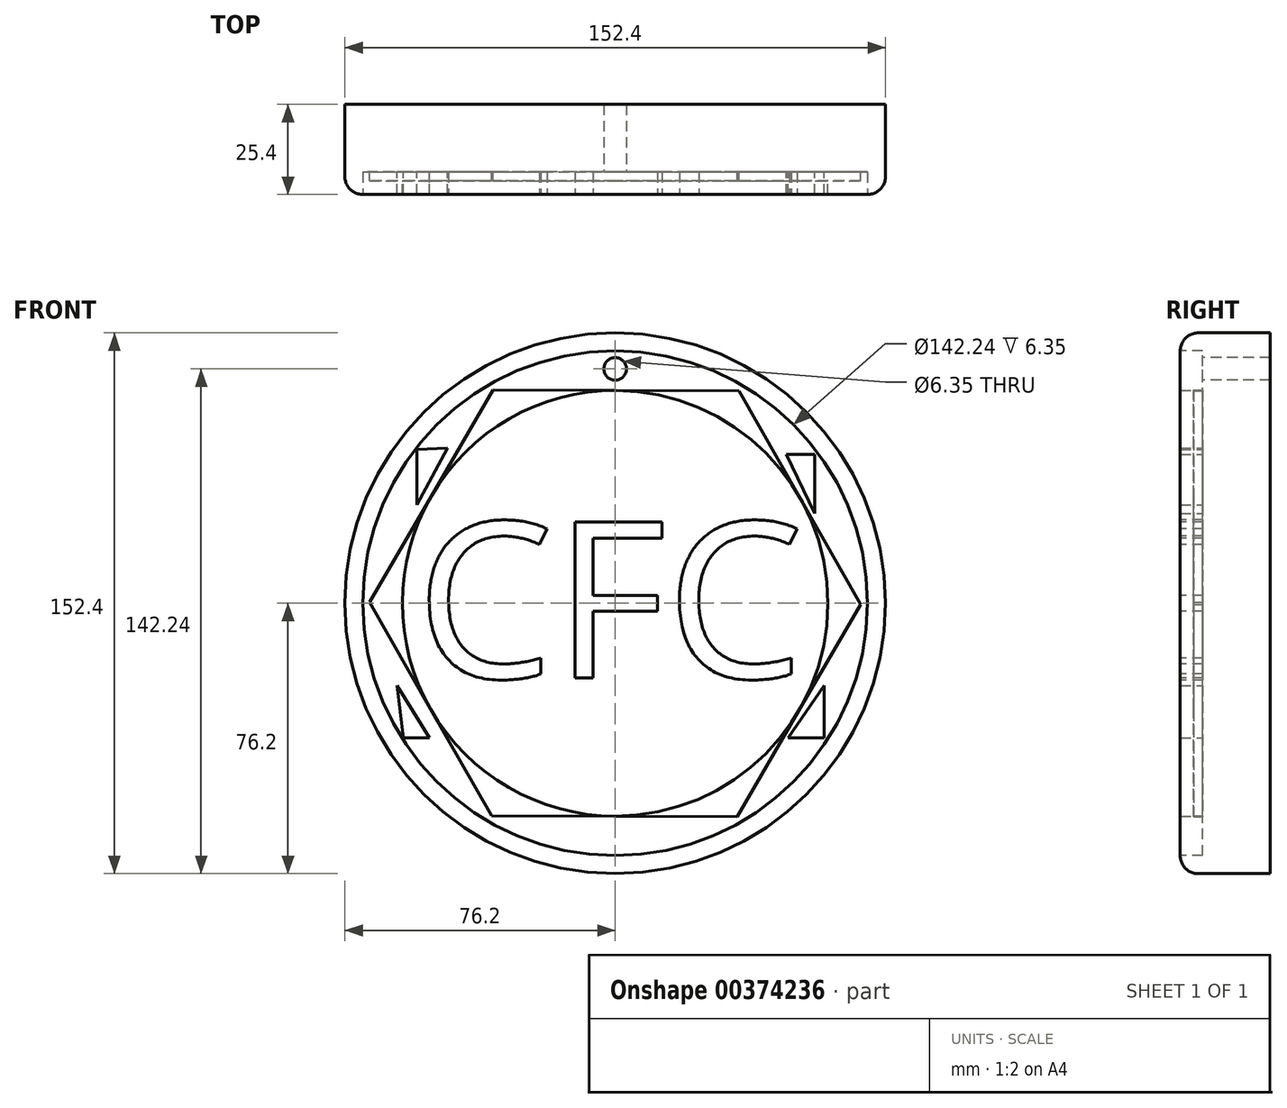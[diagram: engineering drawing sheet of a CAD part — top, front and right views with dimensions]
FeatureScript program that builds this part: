
annotation { "Feature Type Name" : "Feature", "Feature Type Description" : "" }
export const myFeature = defineFeature(function(context is Context, id is Id, definition is map)
    precondition{}
    {
        {
            var Q0;
            Q0=qCreatedBy(makeId("Front.planeOp"),FACE);
            var sketch = newSketch(context, id + "F0", { "sketchPlane" : qUnion([Q0])});
            skCircle(sketch, "E0", {"center": v(0, 0) * mm, "radius": 76.2 * mm});
            skSolve(sketch);
        }
        {
            var Q0;
            Q0 = qSketchRegion(id + "F0", true);
            extrude(context, id + "F1", {"entities" : qUnion([Q0]), "depth" : 25.4 * mm});
        }
        {
            var Q0;
            Q0=makeQuery(id+"F1.opExtrude","CAP_FACE",FACE,{"disambiguationData":[OSD([sQuery(id+"F0.wireOp",EDGE,"E0")])],"isStart":false});
            fillet(context, id + "F2", {"entities" : qUnion([Q0]), "radius" : 5.08 * mm, "tangentPropagation" : true, "allowEdgeOverflow" : false});
        }
        {
            var Q0;
            Q0=makeQuery(id+"F1.opExtrude","CAP_FACE",FACE,{"disambiguationData":[OSD([sQuery(id+"F0.wireOp",EDGE,"E0")])],"isStart":false});
            extrude(context, id + "F3", {"entities" : qUnion([Q0]), "operationType" : NewBodyOperationType.REMOVE, "oppositeDirection" : true, "depth" : 6.35 * mm});
        }
        {
            var Q0;
            Q0=makeQuery(id+"F3.boolean.opBoolean","COPY",FACE,{"derivedFrom":makeQuery(id+"F3.opExtrude","CAP_FACE",FACE,{"disambiguationData":[OSD([sQuery(id+"F0.wireOp",EDGE,"E0")])],"isStart":false})});
            var sketch = newSketch(context, id + "F4", { "sketchPlane" : qUnion([Q0])});
            skLineSegment(sketch, "E1", {"start": v(0, 0) * mm, "end": v(0, 66.04) * mm});
            skCircle(sketch, "E2", {"center": v(0, 66.04) * mm, "radius": 3.18 * mm});
            skSolve(sketch);
        }
        {
            var Q0;
            Q0=makeQuery(id+"F4.imprint","IMPRINT",FACE,{"disambiguationData":[TD([[makeQuery(id+"F4.imprint","IMPRINT",EDGE,{"derivedFrom":sQuery(id+"F4.wireOp",EDGE,"E2")}),-1.0]])]});
            var sketch = newSketch(context, id + "F5", { "sketchPlane" : qUnion([Q0])});
            skCircle(sketch, "E3.cCircle", {"center": v(0, 0) * mm, "radius": 59.98 * mm, "construction": true});
            skLineSegment(sketch, "E3.0", {"start": v(34.87, 59.84) * mm, "end": v(69.26, -0.28) * mm});
            skLineSegment(sketch, "E3.1", {"start": v(69.26, -0.28) * mm, "end": v(34.39, -60.12) * mm});
            skLineSegment(sketch, "E3.2", {"start": v(34.39, -60.12) * mm, "end": v(-34.87, -59.84) * mm});
            skLineSegment(sketch, "E3.3", {"start": v(-34.87, -59.84) * mm, "end": v(-69.26, 0.28) * mm});
            skLineSegment(sketch, "E3.4", {"start": v(-69.26, 0.28) * mm, "end": v(-34.39, 60.12) * mm});
            skLineSegment(sketch, "E3.5", {"start": v(-34.39, 60.12) * mm, "end": v(34.87, 59.84) * mm});
            skPoint(sketch, "E3.0.midPoint", {"position": v(52.06, 29.78) * mm});
            skSolve(sketch);
        }
        {
            var Q0;
            Q0 = qSketchRegion(id + "F5", true);
            extrude(context, id + "F6", {"entities" : qUnion([Q0]), "operationType" : NewBodyOperationType.ADD, "depth" : 2.54 * mm});
        }
        {
            var Q0;
            Q0=makeQuery(id+"F6.opExtrude","CAP_FACE",FACE,{"disambiguationData":[OSD([sQuery(id+"F5.wireOp",EDGE,"E3.0"),sQuery(id+"F5.wireOp",EDGE,"E3.1"),sQuery(id+"F5.wireOp",EDGE,"E3.2"),sQuery(id+"F5.wireOp",EDGE,"E3.3"),sQuery(id+"F5.wireOp",EDGE,"E3.4"),sQuery(id+"F5.wireOp",EDGE,"E3.5")])],"isStart":false});
            var sketch = newSketch(context, id + "F7", { "sketchPlane" : qUnion([Q0])});
            skCircle(sketch, "E4", {"center": v(0, 0) * mm, "radius": 59.98 * mm});
            skSolve(sketch);
        }
        {
            var Q0;
            Q0 = qSketchRegion(id + "F7", true);
            extrude(context, id + "F8", {"entities" : qUnion([Q0]), "operationType" : NewBodyOperationType.ADD, "depth" : 3.8 * mm});
        }
        {
            var Q0;
            Q0=makeQuery(id+"F4.imprint","IMPRINT",FACE,{"disambiguationData":[TD([[makeQuery(id+"F4.imprint","IMPRINT",EDGE,{"derivedFrom":sQuery(id+"F4.wireOp",EDGE,"E2")}),-1.0]])]});
            var sketch = newSketch(context, id + "F9", { "sketchPlane" : qUnion([Q0])});
            skLineSegment(sketch, "E5", {"start": v(-55.9, 43.39) * mm, "end": v(-55.9, 27.7) * mm});
            skLineSegment(sketch, "E6", {"start": v(-55.9, 27.7) * mm, "end": v(-47.33, 43.68) * mm});
            skLineSegment(sketch, "E7", {"start": v(-47.33, 43.68) * mm, "end": v(-55.9, 43.39) * mm});
            skLineSegment(sketch, "E8", {"start": v(-61.52, -23.17) * mm, "end": v(-52.35, -37.96) * mm});
            skLineSegment(sketch, "E9", {"start": v(-52.35, -37.96) * mm, "end": v(-59.75, -37.96) * mm});
            skLineSegment(sketch, "E10", {"start": v(-59.75, -37.96) * mm, "end": v(-61.52, -23.17) * mm});
            skLineSegment(sketch, "E11", {"start": v(48.81, -37.96) * mm, "end": v(58.87, -37.96) * mm});
            skLineSegment(sketch, "E12", {"start": v(58.87, -37.96) * mm, "end": v(58.87, -23.17) * mm});
            skLineSegment(sketch, "E13", {"start": v(58.87, -23.17) * mm, "end": v(48.81, -37.96) * mm});
            skLineSegment(sketch, "E14", {"start": v(48.22, 41.9) * mm, "end": v(56.2, 41.9) * mm});
            skLineSegment(sketch, "E15", {"start": v(56.2, 41.9) * mm, "end": v(56.2, 25.34) * mm});
            skLineSegment(sketch, "E16", {"start": v(56.2, 25.34) * mm, "end": v(48.22, 41.9) * mm});
            skSolve(sketch);
        }
        {
            var Q0;
            Q0=makeQuery(id+"F9.imprint","IMPRINT",FACE,{"disambiguationData":[TD([[makeQuery(id+"F9.imprint","IMPRINT",EDGE,{"derivedFrom":sQuery(id+"F9.wireOp",EDGE,"E5")}),1.0]])]});
            var Q1;
            Q1=makeQuery(id+"F9.imprint","IMPRINT",FACE,{"disambiguationData":[TD([[makeQuery(id+"F9.imprint","IMPRINT",EDGE,{"derivedFrom":sQuery(id+"F9.wireOp",EDGE,"E8")}),-1.0]])]});
            var Q2;
            Q2=makeQuery(id+"F9.imprint","IMPRINT",FACE,{"disambiguationData":[TD([[makeQuery(id+"F9.imprint","IMPRINT",EDGE,{"derivedFrom":sQuery(id+"F9.wireOp",EDGE,"E14")}),-1.0]])]});
            var Q3;
            Q3=makeQuery(id+"F9.imprint","IMPRINT",FACE,{"disambiguationData":[TD([[makeQuery(id+"F9.imprint","IMPRINT",EDGE,{"derivedFrom":sQuery(id+"F9.wireOp",EDGE,"E11")}),1.0]])]});
            extrude(context, id + "F10", {"entities" : qUnion([Q0, Q1, Q2, Q3]), "operationType" : NewBodyOperationType.ADD, "depth" : 6.35 * mm});
        }
        {
            var Q0;
            Q0=makeQuery(id+"F8.opExtrude","CAP_FACE",FACE,{"disambiguationData":[OSD([sQuery(id+"F7.wireOp",EDGE,"E4")])],"isStart":false});
            var sketch = newSketch(context, id + "F11", { "sketchPlane" : qUnion([Q0])});
            skText(sketch, "E17", { "text": "CFC", "fontName": "OpenSans-Regular.ttf"});
            const initialGuessF11  = {"E17": [-0.05617, -0.02103, 1, 0, 0.04427]};
            skSetInitialGuess(sketch, initialGuessF11);
            skSolve(sketch);
        }
        {
            var Q0;
            Q0 = qSketchRegion(id + "F11", true);
            extrude(context, id + "F12", {"entities" : qUnion([Q0]), "operationType" : NewBodyOperationType.REMOVE, "oppositeDirection" : true, "depth" : 6.35 * mm});
        }
        {
            var Q0;
            Q0=makeQuery(id+"F4.imprint","IMPRINT",FACE,{"disambiguationData":[TD([[makeQuery(id+"F4.imprint","IMPRINT",EDGE,{"derivedFrom":sQuery(id+"F4.wireOp",EDGE,"E2")}),1.0]])]});
            extrude(context, id + "F13", {"entities" : qUnion([Q0]), "operationType" : NewBodyOperationType.REMOVE, "oppositeDirection" : true, "depth" : 25.4 * mm});
        }
    });
